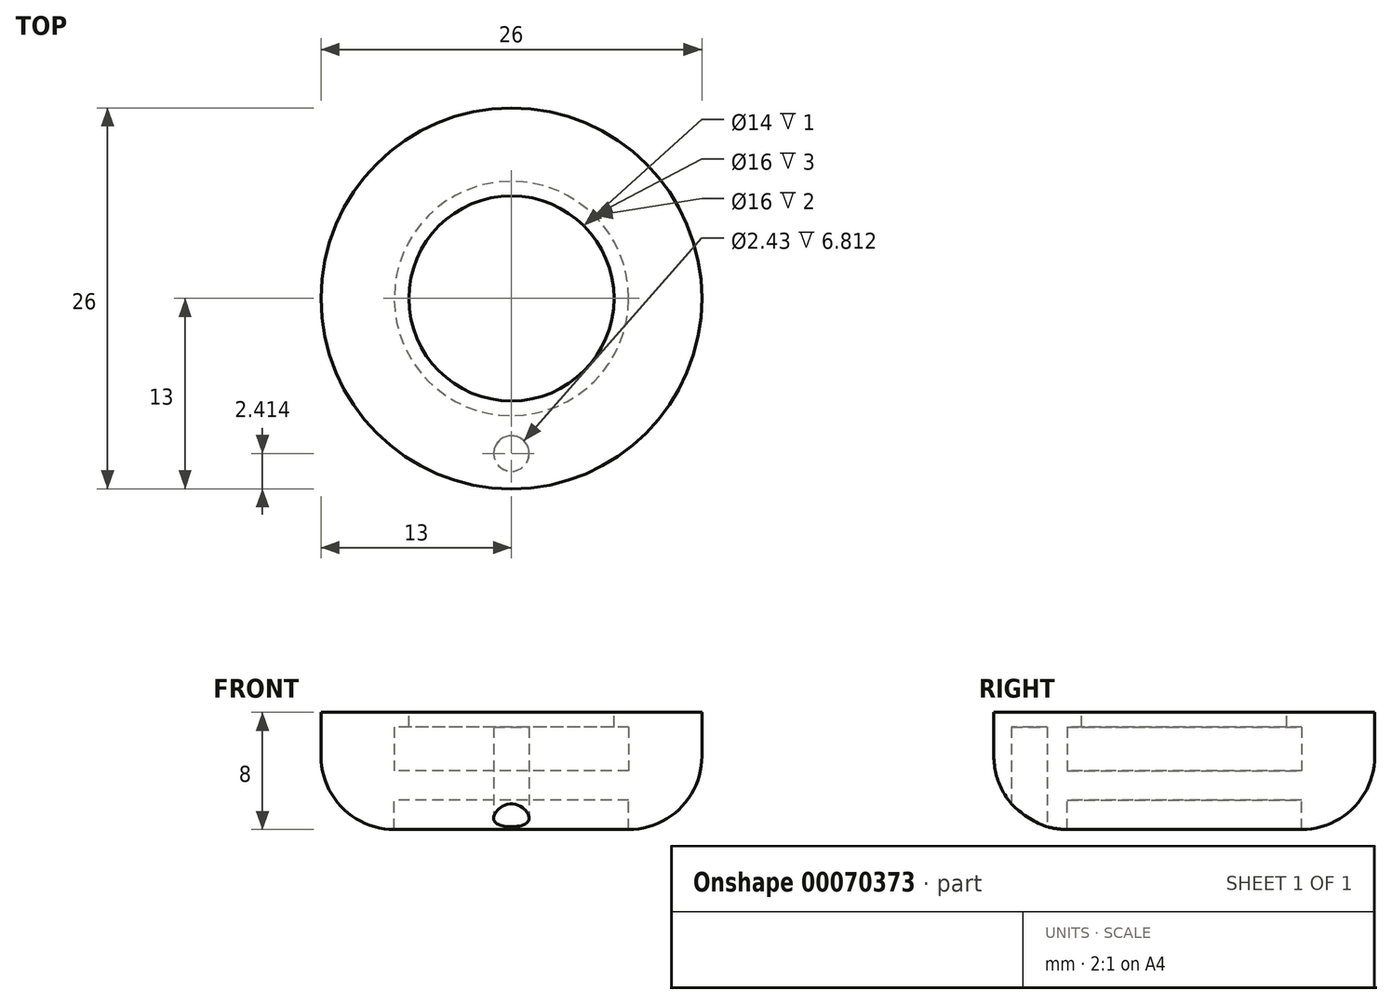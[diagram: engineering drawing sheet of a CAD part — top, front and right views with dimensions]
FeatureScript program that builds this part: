
annotation { "Feature Type Name" : "Feature", "Feature Type Description" : "" }
export const myFeature = defineFeature(function(context is Context, id is Id, definition is map)
    precondition{}
    {
        {
            var Q0;
            Q0=qCreatedBy(makeId("Top.planeOp"),FACE);
            var sketch = newSketch(context, id + "F0", { "sketchPlane" : qUnion([Q0])});
            skCircle(sketch, "E0", {"center": v(0, 0) * mm, "radius": 7 * mm});
            skCircle(sketch, "E1", {"center": v(0, 0) * mm, "radius": 8 * mm});
            skCircle(sketch, "E2", {"center": v(0, 0) * mm, "radius": 13 * mm});
            skCircle(sketch, "E3", {"center": v(0, -10.59) * mm, "radius": 1.21 * mm});
            skSolve(sketch);
        }
        {
            var Q0;
            Q0=makeQuery(id+"F0.imprint","IMPRINT",FACE,{"disambiguationData":[TD([[makeQuery(id+"F0.imprint","IMPRINT",EDGE,{"derivedFrom":sQuery(id+"F0.wireOp",EDGE,"E0")}),1.0]])]});
            var Q1;
            Q1=makeQuery(id+"F0.imprint","IMPRINT",FACE,{"disambiguationData":[TD([[makeQuery(id+"F0.imprint","IMPRINT",EDGE,{"derivedFrom":sQuery(id+"F0.wireOp",EDGE,"E0")}),-1.0]])]});
            var Q2;
            Q2=makeQuery(id+"F0.imprint","IMPRINT",FACE,{"disambiguationData":[TD([[makeQuery(id+"F0.imprint","IMPRINT",EDGE,{"derivedFrom":sQuery(id+"F0.wireOp",EDGE,"E1")}),-1.0]])]});
            extrude(context, id + "F1", {"entities" : qUnion([Q0, Q1, Q2]), "depth" : 2 * mm});
        }
        {
            var Q0;
            Q0=makeQuery(id+"F0.imprint","IMPRINT",FACE,{"disambiguationData":[TD([[makeQuery(id+"F0.imprint","IMPRINT",EDGE,{"derivedFrom":sQuery(id+"F0.wireOp",EDGE,"E1")}),-1.0]])]});
            extrude(context, id + "F2", {"entities" : qUnion([Q0]), "operationType" : NewBodyOperationType.ADD, "depth" : 6 * mm});
        }
        {
            var Q0;
            Q0=makeQuery(id+"F2.opExtrude","CAP_FACE",FACE,{"disambiguationData":[OSD([sQuery(id+"F0.wireOp",EDGE,"E1"),sQuery(id+"F0.wireOp",EDGE,"E2")])],"isStart":false});
            cPlane(context, id + "F3", {"entities" : qUnion([Q0]), "cplaneType" : CPlaneType.OFFSET, "offset" : 0 * mm, "width" : 150 * mm, "height" : 150 * mm});
        }
        {
            var Q0;
            Q0=qCreatedBy(id+"F3.planeOp",FACE);
            var sketch = newSketch(context, id + "F4", { "sketchPlane" : qUnion([Q0])});
            skCircle(sketch, "E4", {"center": v(0, 0) * mm, "radius": 8 * mm});
            skCircle(sketch, "E5", {"center": v(0, 0) * mm, "radius": 7 * mm});
            skCircle(sketch, "E6", {"center": v(0, 0) * mm, "radius": 13 * mm});
            skSolve(sketch);
        }
        {
            var Q0;
            Q0 = qSketchRegion(id + "F4", true);
            var Q1;
            Q1=makeQuery(id+"F4.imprint","IMPRINT",FACE,{"disambiguationData":[TD([[makeQuery(id+"F4.imprint","IMPRINT",EDGE,{"derivedFrom":sQuery(id+"F4.wireOp",EDGE,"E4")}),1.0]])]});
            extrude(context, id + "F5", {"entities" : qUnion([Q0, Q1]), "operationType" : NewBodyOperationType.ADD, "oppositeDirection" : true, "depth" : 1 * mm});
        }
        {
            var Q0;
            Q0=makeQuery(id+"F2.opExtrude","CAP_FACE",FACE,{"disambiguationData":[OSD([sQuery(id+"F0.wireOp",EDGE,"E1"),sQuery(id+"F0.wireOp",EDGE,"E2")])],"isStart":true});
            var Q1;
            Q1=makeQuery(id+"F0.imprint","IMPRINT",FACE,{"disambiguationData":[TD([[makeQuery(id+"F0.imprint","IMPRINT",EDGE,{"derivedFrom":sQuery(id+"F0.wireOp",EDGE,"E0")}),1.0]])]});
            extrude(context, id + "F6", {"entities" : qUnion([Q0, Q1]), "operationType" : NewBodyOperationType.ADD, "depth" : 1 * mm});
        }
        {
            var Q0;
            Q0 = qSketchRegion(id + "F0", true);
            extrude(context, id + "F7", {"entities" : qUnion([Q0]), "operationType" : NewBodyOperationType.ADD, "oppositeDirection" : true, "depth" : 2 * mm});
        }
        {
            var Q0;
            Q0=makeQuery(id+"F7.opExtrude","CAP_EDGE",EDGE,{"disambiguationData":[OSD([sQuery(id+"F0.wireOp",EDGE,"E2")])],"isStart":false});
            fillet(context, id + "F8", {"entities" : qUnion([Q0]), "radius" : 5 * mm, "tangentPropagation" : true, "allowEdgeOverflow" : false});
        }
    });
